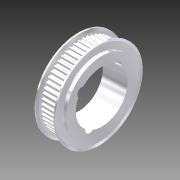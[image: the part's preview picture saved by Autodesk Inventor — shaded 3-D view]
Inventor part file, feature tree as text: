
AUTODESK INVENTOR PART (.ipt)
format: ipt  version: 2011 (Build 150239000, 239)  size: 847,360 bytes
history: native  units: mm
features: imported_body x1, plane x1, extrude x1, pattern_circular x1, sketch x1
ambient origin geometry x8: Origin, YZ Plane, XZ Plane, XY Plane, X Axis, Y Axis, Z Axis, Center Point
bodies: Solid1 (feature_tree)
feature tree (5):
  imported_body  "Base1"
  plane  "Work Plane1"
  extrude  "Extrusion1"  Depth=17.526mm TaperAngle=0.0deg
  pattern_circular  "Circular Pattern1"  Count=56 Angle=360.0deg
  sketch  "Sketch1"  dims[d0=20.0mm d2=1.121997mm d4=17.526mm d5=0.0mm d6=560.0mm d7=360.0deg]
